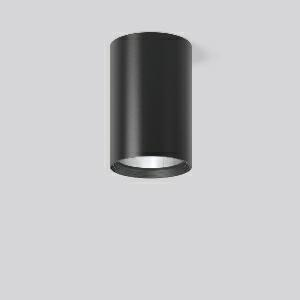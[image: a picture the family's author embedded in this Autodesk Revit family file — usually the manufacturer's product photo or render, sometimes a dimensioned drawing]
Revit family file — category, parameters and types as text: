
# Revit family: heledon_maxi_a_931223_003_2_76_397b
name_source: partatom
category: Lighting Fixtures
units: mm (PartAtom-declared; Revit-internal decimal feet)

## family parameters
Cut with Voids When Loaded = No
Host = Face
Light Source = No
Part Type = Normal
Room Calculation Point = No
Round Connector Dimension = Use Diameter
Shared = No

## types (1)
- HELEDON maxi A (1 x LED Modul 927, 4000 lm, 2700)
    Apparent Load = 35 VA
    Approval mark = CE
    CIE Flux Codes = 100 100 100 100 100
    Color Rendering = 92
    Color Temperature = 2700
    Default Elevation = 1800 mm
    Description = Series: HELEDON maxi
Cylindrical surface-mounted downlight. Housing: die-cast aluminium, powder-coated. Internal ceiling frame polycarbonate with bayonet mounting. Black plastic ring and recessed LED to prevent glare from the side. Optical assembly with reflector made of MIRO-Silver with 98% total light reflection for outstanding efficiency - can be changed without tools. Best colour rendering index Ra>90. Suitable for Ceiling mounting. Easy installation with a separate ceiling frame with bayonet mounting and plug connection. Driver integrated. Connected via plug-in connector. High quality converter without flickering and stroboscopic effect. The following accessories can be mounted without use of tools: interchangeable lenses, decorative glasses, honeycomb louvre, clear and frosted diffusers, white interchangeable plastic ring. 
Colour: deep black, matt (RAL 9005)
Diameter: 123 mm
Height: 183 mm
Lamp: LED
Socket: without socket
Colour temperature: 2700K
Colour rendering index (CRI): 92
System power: 35 W
Rated luminous flux: 4000 lm
Luminous efficiency: 114 lm/W
Control gear: Converter, dimmable, DALI
Protection class: I
Type of protection: IP 20
    Height = 183 mm
    Lamp = 1 x LED Modul 927
    Lamp Light Flux = 4000 lm
    Lamp count = 1
    Length = 123 mm
    Lifetime = 50000 h
    Luminous efficacy = 114 lm/W
    Manufacturer = RZB
    ModVariant = No
    Model = 931223.003.2.76
    Mounting Place = Ceiling
    Mounting Type = Surface mounted
    Number of Poles = 1
    OnlyDefault = Yes
    Power Factor = 1
    Product Name = HELEDON maxi A
    Product group = Surface mounted downlights
    ProductGroupID = 302
    Protection Class = Protection class I
    Protection Degree = IP 20
    RLX_Detail_Level = 1
    RLX_Emergency_Light_Flux = 0 lm
    RLX_Emergency_Type = 0
    RLX_Emergency_Type_DB = No
    RlxData = <blob elided: 96761 chars, md5=757d81f8>
    Socket = socket
    Standby Power = 0 W
    System Light Flux = 4000 lm
    System Power = 35 W
    Type Comments = Product without accessories
    Type Image = 931192.003.jpg
    URL = http://relux.com
    VarID = ---
    Voltage = 230 V
    Voltage Range = 220-240 V
    Weight = 0.00 kg
    Width = 0 mm  [stored 0 ft]

note: [stored X ft] marks values corroborated as IEEE doubles in the binary element streams (Revit-internal decimal feet)

## geometry (parser evidence)
native form markers: Blend x4, Sweep x11
no freeform markers — native parametric forms only
